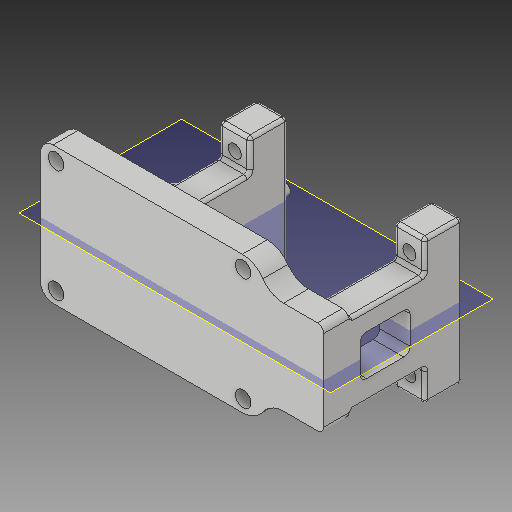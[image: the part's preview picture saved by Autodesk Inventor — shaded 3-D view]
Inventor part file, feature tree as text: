
AUTODESK INVENTOR PART (.ipt)
format: ipt  version: 2019 (Build 230136000, 136)  size: 348,160 bytes
history: native  units: mm
features: sketch x10, other x3, plane x1
ambient origin geometry x8: Origin, YZ Plane, XZ Plane, XY Plane, X Axis, Y Axis, Z Axis, Center Point
bodies: Solid1 (feature_tree)
feature tree (14):
  other  "servo_hold.ipt"
  other  "Solid1::servo_hold.ipt"
  other  "TaggingFeature1"
  sketch  "Sketch1"  dims[d0=10.0mm]
  sketch  "Sketch2"
  sketch  "Sketch3"
  sketch  "Sketch5"
  sketch  "Sketch6"
  sketch  "Sketch7"
  sketch  "Sketch8"
  sketch  "Sketch10"
  sketch  "Sketch12"
  sketch  "Sketch14"
  plane  "Work Plane1"
